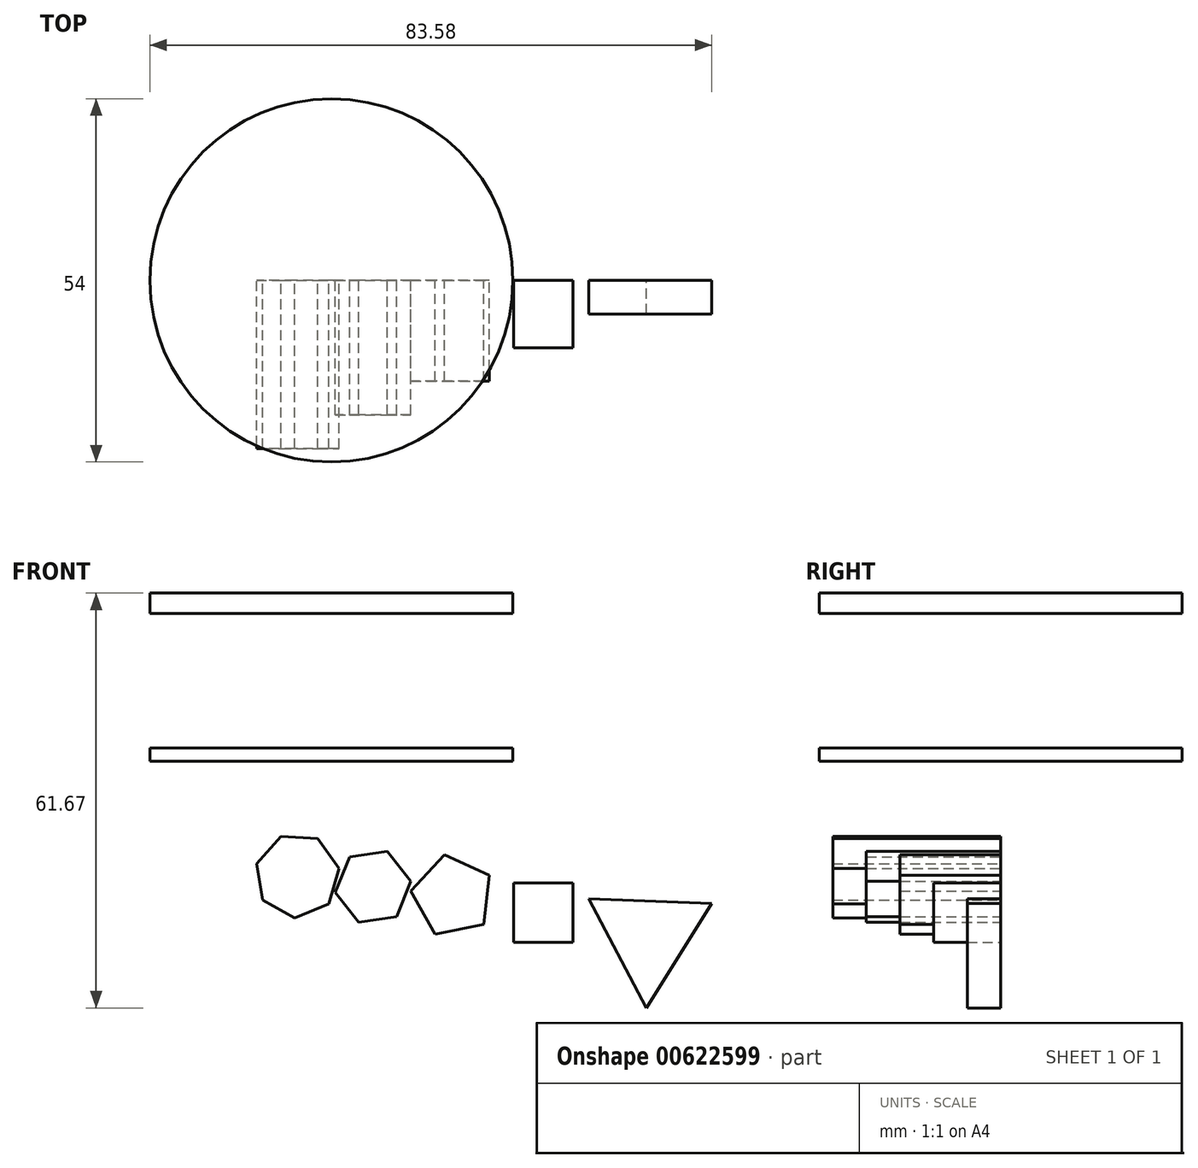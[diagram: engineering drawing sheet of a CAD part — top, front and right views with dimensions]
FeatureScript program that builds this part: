
annotation { "Feature Type Name" : "Feature", "Feature Type Description" : "" }
export const myFeature = defineFeature(function(context is Context, id is Id, definition is map)
    precondition{}
    {
        {
            var Q0;
            Q0=qCreatedBy(makeId("Top.planeOp"),FACE);
            var sketch = newSketch(context, id + "F0", { "sketchPlane" : qUnion([Q0])});
            skCircle(sketch, "E0", {"center": v(0, 0) * mm, "radius": 27 * mm});
            skSolve(sketch);
        }
        {
            var Q0;
            Q0=makeQuery(id+"F0.imprint","IMPRINT",FACE,{"disambiguationData":[TD([[makeQuery(id+"F0.imprint","IMPRINT",EDGE,{"derivedFrom":sQuery(id+"F0.wireOp",EDGE,"E0")}),1.0]])]});
            extrude(context, id + "F1", {"entities" : qUnion([Q0]), "oppositeDirection" : true, "depth" : 2 * mm, "offsetDistance" : 25 * mm});
        }
        {
            var Q0;
            Q0 = qSketchRegion(id + "F0", true);
            extrude(context, id + "F2", {"entities" : qUnion([Q0]), "depth" : 23 * mm, "offsetDistance" : 25 * mm});
        }
        {
            var Q0;
            Q0 = qSketchRegion(id + "F0", true);
            extrude(context, id + "F3", {"entities" : qUnion([Q0]), "operationType" : NewBodyOperationType.REMOVE, "depth" : 20 * mm, "offsetDistance" : 25 * mm});
        }
        {
            var Q0;
            Q0=qCreatedBy(makeId("Front.planeOp"),FACE);
            var sketch = newSketch(context, id + "F4", { "sketchPlane" : qUnion([Q0])});
            skCircle(sketch, "E1.cCircle", {"center": v(47.22, -28.09) * mm, "radius": 5.3 * mm, "construction": true});
            skLineSegment(sketch, "E1.0", {"start": v(46.83, -38.67) * mm, "end": v(38.25, -22.46) * mm});
            skLineSegment(sketch, "E1.1", {"start": v(38.25, -22.46) * mm, "end": v(56.58, -23.13) * mm});
            skLineSegment(sketch, "E1.2", {"start": v(56.58, -23.13) * mm, "end": v(46.83, -38.67) * mm});
            skPoint(sketch, "E1.0.midPoint", {"position": v(42.54, -30.56) * mm});
            skSolve(sketch);
        }
        {
            var Q0;
            Q0=makeQuery(id+"F4.imprint","IMPRINT",FACE,{"disambiguationData":[TD([[makeQuery(id+"F4.imprint","IMPRINT",EDGE,{"derivedFrom":sQuery(id+"F4.wireOp",EDGE,"E1.0")}),-1.0]])]});
            extrude(context, id + "F5", {"entities" : qUnion([Q0]), "depth" : 5 * mm, "offsetDistance" : 25 * mm});
        }
        {
            var Q0;
            Q0=qCreatedBy(makeId("Front.planeOp"),FACE);
            var sketch = newSketch(context, id + "F6", { "sketchPlane" : qUnion([Q0])});
            skCircle(sketch, "E2.cCircle", {"center": v(31.53, -24.5) * mm, "radius": 4.4 * mm, "construction": true});
            skLineSegment(sketch, "E2.0", {"start": v(35.93, -28.91) * mm, "end": v(27.12, -28.91) * mm});
            skLineSegment(sketch, "E2.1", {"start": v(27.12, -28.91) * mm, "end": v(27.12, -20.1) * mm});
            skLineSegment(sketch, "E2.2", {"start": v(27.12, -20.1) * mm, "end": v(35.93, -20.1) * mm});
            skLineSegment(sketch, "E2.3", {"start": v(35.93, -20.1) * mm, "end": v(35.93, -28.91) * mm});
            skPoint(sketch, "E2.0.midPoint", {"position": v(31.53, -28.91) * mm});
            skSolve(sketch);
        }
        {
            var Q0;
            Q0=makeQuery(id+"F6.imprint","IMPRINT",FACE,{"disambiguationData":[TD([[makeQuery(id+"F6.imprint","IMPRINT",EDGE,{"derivedFrom":sQuery(id+"F6.wireOp",EDGE,"E2.0")}),-1.0]])]});
            extrude(context, id + "F7", {"entities" : qUnion([Q0]), "depth" : 10 * mm, "offsetDistance" : 25 * mm});
        }
        {
            var Q0;
            Q0=qCreatedBy(makeId("Front.planeOp"),FACE);
            var sketch = newSketch(context, id + "F8", { "sketchPlane" : qUnion([Q0])});
            skCircle(sketch, "E3.cCircle", {"center": v(18.04, -22.03) * mm, "radius": 5.05 * mm, "construction": true});
            skLineSegment(sketch, "E3.0", {"start": v(15.43, -27.7) * mm, "end": v(11.83, -21.3) * mm});
            skLineSegment(sketch, "E3.1", {"start": v(11.83, -21.3) * mm, "end": v(16.8, -15.9) * mm});
            skLineSegment(sketch, "E3.2", {"start": v(16.8, -15.9) * mm, "end": v(23.48, -18.96) * mm});
            skLineSegment(sketch, "E3.3", {"start": v(23.48, -18.96) * mm, "end": v(22.63, -26.26) * mm});
            skLineSegment(sketch, "E3.4", {"start": v(22.63, -26.26) * mm, "end": v(15.43, -27.7) * mm});
            skPoint(sketch, "E3.0.midPoint", {"position": v(13.63, -24.5) * mm});
            skSolve(sketch);
        }
        {
            var Q0;
            Q0=makeQuery(id+"F8.imprint","IMPRINT",FACE,{"disambiguationData":[TD([[makeQuery(id+"F8.imprint","IMPRINT",EDGE,{"derivedFrom":sQuery(id+"F8.wireOp",EDGE,"E3.0")}),-1.0]])]});
            extrude(context, id + "F9", {"entities" : qUnion([Q0]), "depth" : 15 * mm, "offsetDistance" : 25 * mm});
        }
        {
            var Q0;
            Q0=qCreatedBy(makeId("Front.planeOp"),FACE);
            var sketch = newSketch(context, id + "F10", { "sketchPlane" : qUnion([Q0])});
            skCircle(sketch, "E4.cCircle", {"center": v(6.2, -20.65) * mm, "radius": 4.9 * mm, "construction": true});
            skLineSegment(sketch, "E4.0", {"start": v(4.09, -25.9) * mm, "end": v(0.6, -21.45) * mm});
            skLineSegment(sketch, "E4.1", {"start": v(0.6, -21.45) * mm, "end": v(2.7, -16.2) * mm});
            skLineSegment(sketch, "E4.2", {"start": v(2.7, -16.2) * mm, "end": v(8.3, -15.4) * mm});
            skLineSegment(sketch, "E4.3", {"start": v(8.3, -15.4) * mm, "end": v(11.8, -19.85) * mm});
            skLineSegment(sketch, "E4.4", {"start": v(11.8, -19.85) * mm, "end": v(9.7, -25.1) * mm});
            skLineSegment(sketch, "E4.5", {"start": v(9.7, -25.1) * mm, "end": v(4.09, -25.9) * mm});
            skPoint(sketch, "E4.0.midPoint", {"position": v(2.34, -23.68) * mm});
            skSolve(sketch);
        }
        {
            var Q0;
            Q0=makeQuery(id+"F10.imprint","IMPRINT",FACE,{"disambiguationData":[TD([[makeQuery(id+"F10.imprint","IMPRINT",EDGE,{"derivedFrom":sQuery(id+"F10.wireOp",EDGE,"E4.0")}),-1.0]])]});
            extrude(context, id + "F11", {"entities" : qUnion([Q0]), "depth" : 20 * mm, "offsetDistance" : 25 * mm});
        }
        {
            var Q0;
            Q0=qCreatedBy(makeId("Front.planeOp"),FACE);
            var sketch = newSketch(context, id + "F12", { "sketchPlane" : qUnion([Q0])});
            skCircle(sketch, "E5.cCircle", {"center": v(-5.1, -19) * mm, "radius": 5.67 * mm, "construction": true});
            skLineSegment(sketch, "E5.0", {"start": v(-5.46, -25.28) * mm, "end": v(-10.23, -22.63) * mm});
            skLineSegment(sketch, "E5.1", {"start": v(-10.23, -22.63) * mm, "end": v(-11.14, -17.24) * mm});
            skLineSegment(sketch, "E5.2", {"start": v(-11.14, -17.24) * mm, "end": v(-7.49, -13.18) * mm});
            skLineSegment(sketch, "E5.3", {"start": v(-7.49, -13.18) * mm, "end": v(-2.04, -13.5) * mm});
            skLineSegment(sketch, "E5.4", {"start": v(-2.04, -13.5) * mm, "end": v(1.11, -17.96) * mm});
            skLineSegment(sketch, "E5.5", {"start": v(1.11, -17.96) * mm, "end": v(-0.41, -23.2) * mm});
            skLineSegment(sketch, "E5.6", {"start": v(-0.41, -23.2) * mm, "end": v(-5.46, -25.28) * mm});
            skPoint(sketch, "E5.0.midPoint", {"position": v(-7.85, -23.96) * mm});
            skSolve(sketch);
        }
        {
            var Q0;
            Q0=makeQuery(id+"F12.imprint","IMPRINT",FACE,{"disambiguationData":[TD([[makeQuery(id+"F12.imprint","IMPRINT",EDGE,{"derivedFrom":sQuery(id+"F12.wireOp",EDGE,"E5.0")}),-1.0]])]});
            extrude(context, id + "F13", {"entities" : qUnion([Q0]), "depth" : 25 * mm, "offsetDistance" : 25 * mm});
        }
    });
